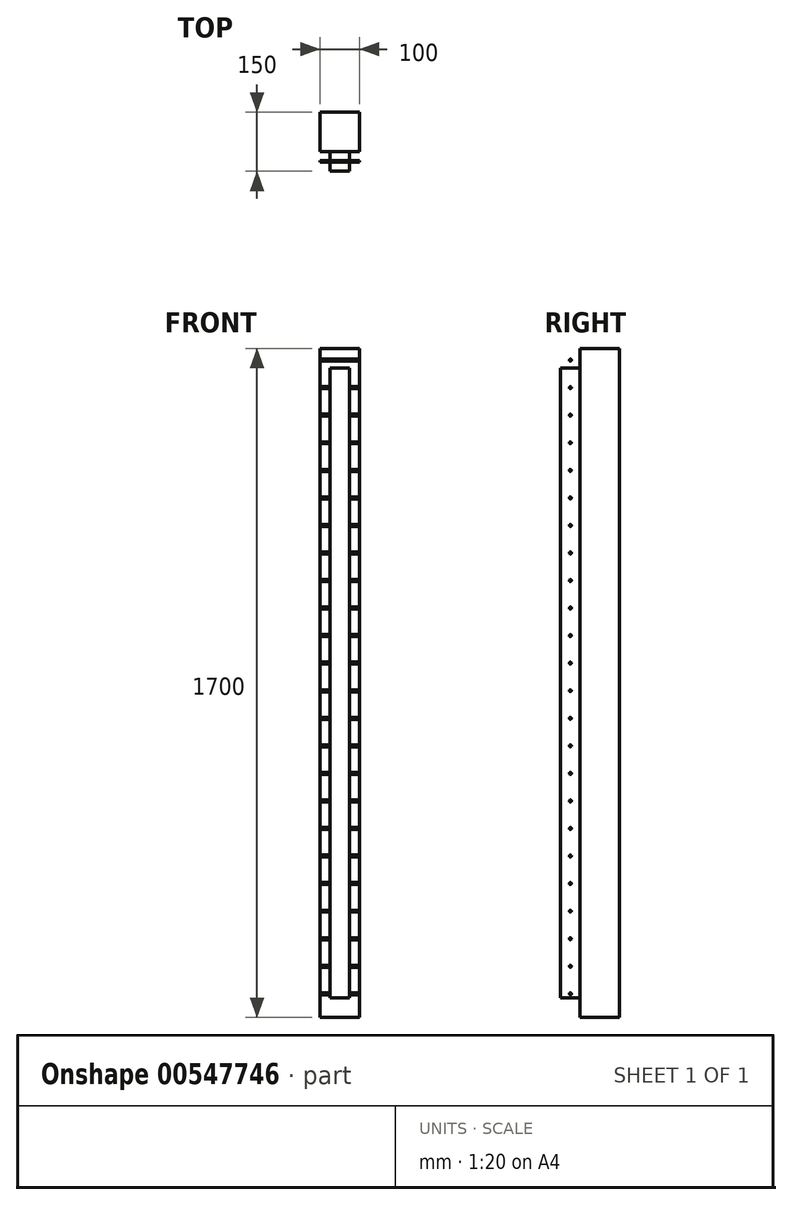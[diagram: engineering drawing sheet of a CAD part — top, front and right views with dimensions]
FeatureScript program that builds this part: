
annotation { "Feature Type Name" : "Feature", "Feature Type Description" : "" }
export const myFeature = defineFeature(function(context is Context, id is Id, definition is map)
    precondition{}
    {
        {
            var Q0;
            Q0=qCreatedBy(makeId("Front.planeOp"),FACE);
            var sketch = newSketch(context, id + "F0", { "sketchPlane" : qUnion([Q0])});
            skLineSegment(sketch, "E0.bottom", {"start": v(50, 850) * mm, "end": v(-50, 850) * mm});
            skLineSegment(sketch, "E0.top", {"start": v(50, -850) * mm, "end": v(-50, -850) * mm});
            skLineSegment(sketch, "E0.left", {"start": v(50, 850) * mm, "end": v(50, -850) * mm});
            skLineSegment(sketch, "E0.right", {"start": v(-50, 850) * mm, "end": v(-50, -850) * mm});
            skPoint(sketch, "E0.middle", {"position": v(0, 0) * mm});
            skSolve(sketch);
        }
        {
            var Q0;
            Q0=makeQuery(id+"F0.imprint","IMPRINT",FACE,{"disambiguationData":[TD([[makeQuery(id+"F0.imprint","IMPRINT",EDGE,{"derivedFrom":sQuery(id+"F0.wireOp",EDGE,"E0.bottom")}),1.0]])]});
            extrude(context, id + "F1", {"entities" : qUnion([Q0]), "depth" : 100 * mm, "offsetDistance" : 25 * mm});
        }
        {
            var Q0;
            Q0=makeQuery(id+"F1.opExtrude","CAP_FACE",FACE,{"disambiguationData":[OSD([sQuery(id+"F0.wireOp",EDGE,"E0.bottom"),sQuery(id+"F0.wireOp",EDGE,"E0.top"),sQuery(id+"F0.wireOp",EDGE,"E0.left"),sQuery(id+"F0.wireOp",EDGE,"E0.right")])],"isStart":false});
            var sketch = newSketch(context, id + "F2", { "sketchPlane" : qUnion([Q0])});
            skPoint(sketch, "E1.middle", {"position": v(0, 0) * mm});
            skLineSegment(sketch, "E2.bottom", {"start": v(25, 800) * mm, "end": v(-25, 800) * mm});
            skLineSegment(sketch, "E2.top", {"start": v(25, -800) * mm, "end": v(-25, -800) * mm});
            skLineSegment(sketch, "E2.left", {"start": v(25, 800) * mm, "end": v(25, -800) * mm});
            skLineSegment(sketch, "E2.right", {"start": v(-25, 800) * mm, "end": v(-25, -800) * mm});
            skSolve(sketch);
        }
        {
            var Q0;
            Q0 = qSketchRegion(id + "F2", true);
            extrude(context, id + "F3", {"entities" : qUnion([Q0]), "operationType" : NewBodyOperationType.ADD, "depth" : 50 * mm, "offsetDistance" : 25 * mm});
        }
        {
            var Q0;
            Q0=makeQuery(id+"F3.opExtrude","SWEPT_FACE",FACE,{"disambiguationData":[OSD([sQuery(id+"F2.wireOp",EDGE,"E2.right")])]});
            var sketch = newSketch(context, id + "F4", { "sketchPlane" : qUnion([Q0])});
            skCircle(sketch, "E3", {"center": v(125, -790) * mm, "radius": 2.5 * mm});
            skLineSegment(sketch, "E4", {"start": v(100, 0) * mm, "end": v(150, 0) * mm});
            skLineSegment(sketch, "E5", {"start": v(125, -800) * mm, "end": v(125, 800) * mm, "construction": true});
            skCircle(sketch, "E6.0.1.0", {"center": v(125, -720) * mm, "radius": 2.5 * mm});
            skCircle(sketch, "E6.0.2.0", {"center": v(125, -650) * mm, "radius": 2.5 * mm});
            skCircle(sketch, "E6.0.3.0", {"center": v(125, -580) * mm, "radius": 2.5 * mm});
            skCircle(sketch, "E6.0.4.0", {"center": v(125, -510) * mm, "radius": 2.5 * mm});
            skCircle(sketch, "E6.0.5.0", {"center": v(125, -440) * mm, "radius": 2.5 * mm});
            skCircle(sketch, "E6.0.6.0", {"center": v(125, -370) * mm, "radius": 2.5 * mm});
            skCircle(sketch, "E6.0.7.0", {"center": v(125, -300) * mm, "radius": 2.5 * mm});
            skCircle(sketch, "E6.0.8.0", {"center": v(125, -230) * mm, "radius": 2.5 * mm});
            skCircle(sketch, "E6.0.9.0", {"center": v(125, -160) * mm, "radius": 2.5 * mm});
            skCircle(sketch, "E6.0.10.0", {"center": v(125, -90) * mm, "radius": 2.5 * mm});
            skCircle(sketch, "E6.0.11.0", {"center": v(125, -20) * mm, "radius": 2.5 * mm});
            skCircle(sketch, "E6.0.12.0", {"center": v(125, 50) * mm, "radius": 2.5 * mm});
            skCircle(sketch, "E6.0.13.0", {"center": v(125, 120) * mm, "radius": 2.5 * mm});
            skCircle(sketch, "E6.0.14.0", {"center": v(125, 190) * mm, "radius": 2.5 * mm});
            skCircle(sketch, "E6.0.15.0", {"center": v(125, 260) * mm, "radius": 2.5 * mm});
            skCircle(sketch, "E6.0.16.0", {"center": v(125, 330) * mm, "radius": 2.5 * mm});
            skCircle(sketch, "E6.0.17.0", {"center": v(125, 400) * mm, "radius": 2.5 * mm});
            skCircle(sketch, "E6.0.18.0", {"center": v(125, 470) * mm, "radius": 2.5 * mm});
            skCircle(sketch, "E6.0.19.0", {"center": v(125, 540) * mm, "radius": 2.5 * mm});
            skCircle(sketch, "E6.0.20.0", {"center": v(125, 610) * mm, "radius": 2.5 * mm});
            skCircle(sketch, "E6.0.21.0", {"center": v(125, 680) * mm, "radius": 2.5 * mm});
            skCircle(sketch, "E6.0.22.0", {"center": v(125, 750) * mm, "radius": 2.5 * mm});
            skCircle(sketch, "E6.0.23.0", {"center": v(125, 820) * mm, "radius": 2.5 * mm});
            skLineSegment(sketch, "E6.direction1", {"start": v(125, -790) * mm, "end": v(194, -790) * mm, "construction": true});
            skLineSegment(sketch, "E6.direction2", {"start": v(125, -790) * mm, "end": v(125, -720) * mm, "construction": true});
            skSolve(sketch);
        }
        {
            var Q0;
            Q0 = qSketchRegion(id + "F4", true);
            extrude(context, id + "F5", {"entities" : qUnion([Q0]), "operationType" : NewBodyOperationType.ADD, "depth" : 25 * mm, "offsetDistance" : 25 * mm, "hasSecondDirection" : true, "secondDirectionOppositeDirection" : true, "secondDirectionDepth" : 75 * mm});
        }
    });
